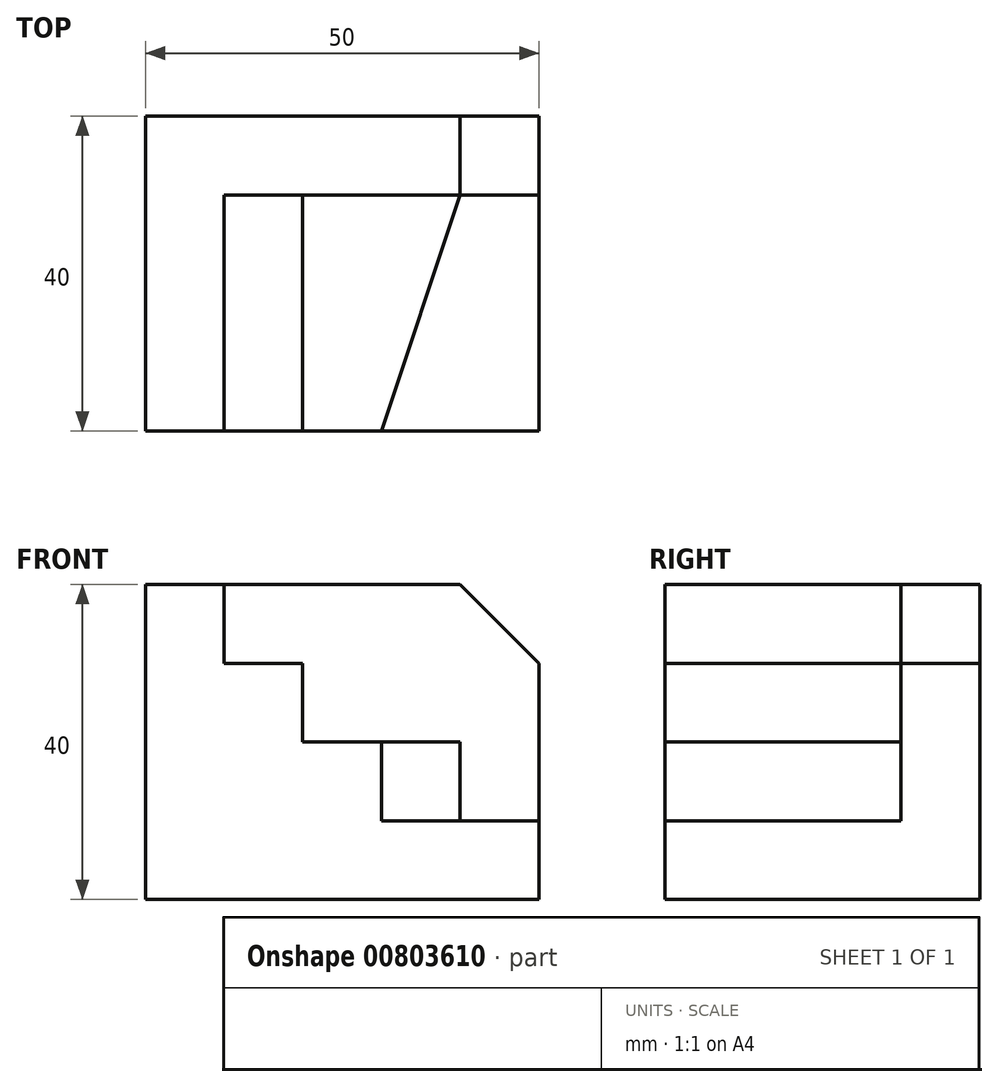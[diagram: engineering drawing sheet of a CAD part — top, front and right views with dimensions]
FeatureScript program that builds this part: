
annotation { "Feature Type Name" : "Feature", "Feature Type Description" : "" }
export const myFeature = defineFeature(function(context is Context, id is Id, definition is map)
    precondition{}
    {
        {
            var Q0;
            Q0=qCreatedBy(makeId("Top.planeOp"),FACE);
            var sketch = newSketch(context, id + "F0", { "sketchPlane" : qUnion([Q0])});
            skLineSegment(sketch, "E0.bottom", {"start": v(0, 0) * mm, "end": v(50, 0) * mm});
            skLineSegment(sketch, "E0.top", {"start": v(0, 40) * mm, "end": v(50, 40) * mm});
            skLineSegment(sketch, "E0.right", {"start": v(50, 0) * mm, "end": v(50, 40) * mm});
            skLineSegment(sketch, "E1", {"start": v(0, 0) * mm, "end": v(0, 40) * mm});
            skLineSegment(sketch, "E2", {"start": v(50, 30) * mm, "end": v(10, 30) * mm});
            skLineSegment(sketch, "E3", {"start": v(10, 30) * mm, "end": v(10, 0) * mm});
            skLineSegment(sketch, "E4", {"start": v(20, 30) * mm, "end": v(20, 0) * mm});
            skLineSegment(sketch, "E5", {"start": v(40, 30) * mm, "end": v(30, 0) * mm});
            skSolve(sketch);
        }
        {
            var Q0;
            {var subQ2=sQuery(id+"F0.wireOp",EDGE,"E0.top");Q0=makeQuery(id+"F0.imprint","IMPRINT",FACE,{"disambiguationData":[TD([[makeQuery(id+"F0.imprint","IMPRINT",EDGE,{"derivedFrom":subQ2}),-1.0]])]});}
            extrude(context, id + "F1", {"entities" : qUnion([Q0]), "depth" : 40 * mm, "offsetDistance" : 25 * mm});
        }
        {
            var Q0;
            {var subQ0=sQuery(id+"F0.wireOp",EDGE,"E3");Q0=makeQuery(id+"F0.imprint","IMPRINT",FACE,{"disambiguationData":[TD([[makeQuery(id+"F0.imprint","IMPRINT",EDGE,{"derivedFrom":subQ0}),1.0]])]});}
            extrude(context, id + "F2", {"entities" : qUnion([Q0]), "operationType" : NewBodyOperationType.ADD, "depth" : 30 * mm, "offsetDistance" : 25 * mm});
        }
        {
            var Q0;
            {var subQ0=sQuery(id+"F0.wireOp",EDGE,"E4");Q0=makeQuery(id+"F0.imprint","IMPRINT",FACE,{"disambiguationData":[TD([[makeQuery(id+"F0.imprint","IMPRINT",EDGE,{"derivedFrom":subQ0}),1.0]])]});}
            extrude(context, id + "F3", {"entities" : qUnion([Q0]), "operationType" : NewBodyOperationType.ADD, "depth" : 20 * mm, "offsetDistance" : 25 * mm});
        }
        {
            var Q0;
            {var subQ3=sQuery(id+"F0.wireOp",EDGE,"E5");Q0=makeQuery(id+"F0.imprint","IMPRINT",FACE,{"disambiguationData":[TD([[makeQuery(id+"F0.imprint","IMPRINT",EDGE,{"derivedFrom":subQ3}),1.0]])]});}
            extrude(context, id + "F4", {"entities" : qUnion([Q0]), "operationType" : NewBodyOperationType.ADD, "depth" : 10 * mm, "offsetDistance" : 25 * mm});
        }
        {
            var Q0;
            Q0=makeQuery(id+"F1.opExtrude","CAP_EDGE",EDGE,{"disambiguationData":[OSD([sQuery(id+"F0.wireOp",EDGE,"E0.right")])],"isStart":false});
            chamfer(context, id + "F5", {"entities" : qUnion([Q0]), "width" : 10 * mm, "tangentPropagation" : true});
        }
    });
